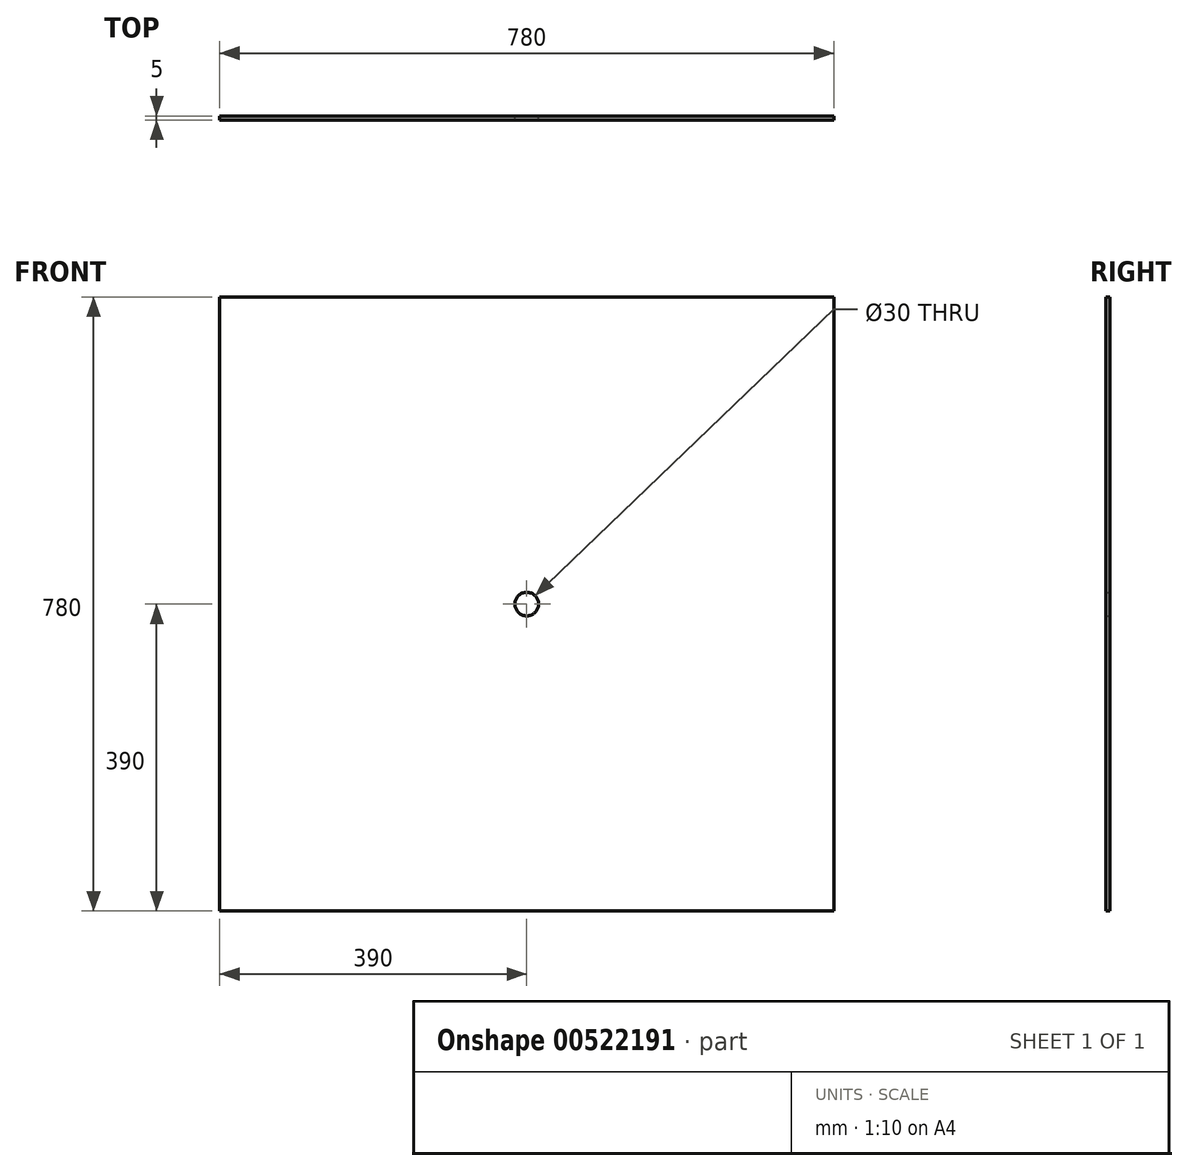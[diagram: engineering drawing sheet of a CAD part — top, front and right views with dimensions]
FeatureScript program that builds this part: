
annotation { "Feature Type Name" : "Feature", "Feature Type Description" : "" }
export const myFeature = defineFeature(function(context is Context, id is Id, definition is map)
    precondition{}
    {
        {
            var Q0;
            Q0=qCreatedBy(makeId("Front.planeOp"),FACE);
            var sketch = newSketch(context, id + "F0", { "sketchPlane" : qUnion([Q0])});
            skLineSegment(sketch, "E0.bottom", {"start": v(0, 0) * mm, "end": v(780, 0) * mm});
            skLineSegment(sketch, "E0.top", {"start": v(0, 780) * mm, "end": v(780, 780) * mm});
            skLineSegment(sketch, "E0.left", {"start": v(0, 0) * mm, "end": v(0, 780) * mm});
            skLineSegment(sketch, "E0.right", {"start": v(780, 0) * mm, "end": v(780, 780) * mm});
            skCircle(sketch, "E1", {"center": v(390, 390) * mm, "radius": 15 * mm});
            skSolve(sketch);
        }
        {
            var Q0;
            Q0=makeQuery(id+"F0.imprint","IMPRINT",FACE,{"disambiguationData":[TD([[makeQuery(id+"F0.imprint","IMPRINT",EDGE,{"derivedFrom":sQuery(id+"F0.wireOp",EDGE,"E0.bottom")}),1.0]])]});
            extrude(context, id + "F1", {"entities" : qUnion([Q0]), "depth" : 5 * mm, "offsetDistance" : 25.4 * mm});
        }
    });
